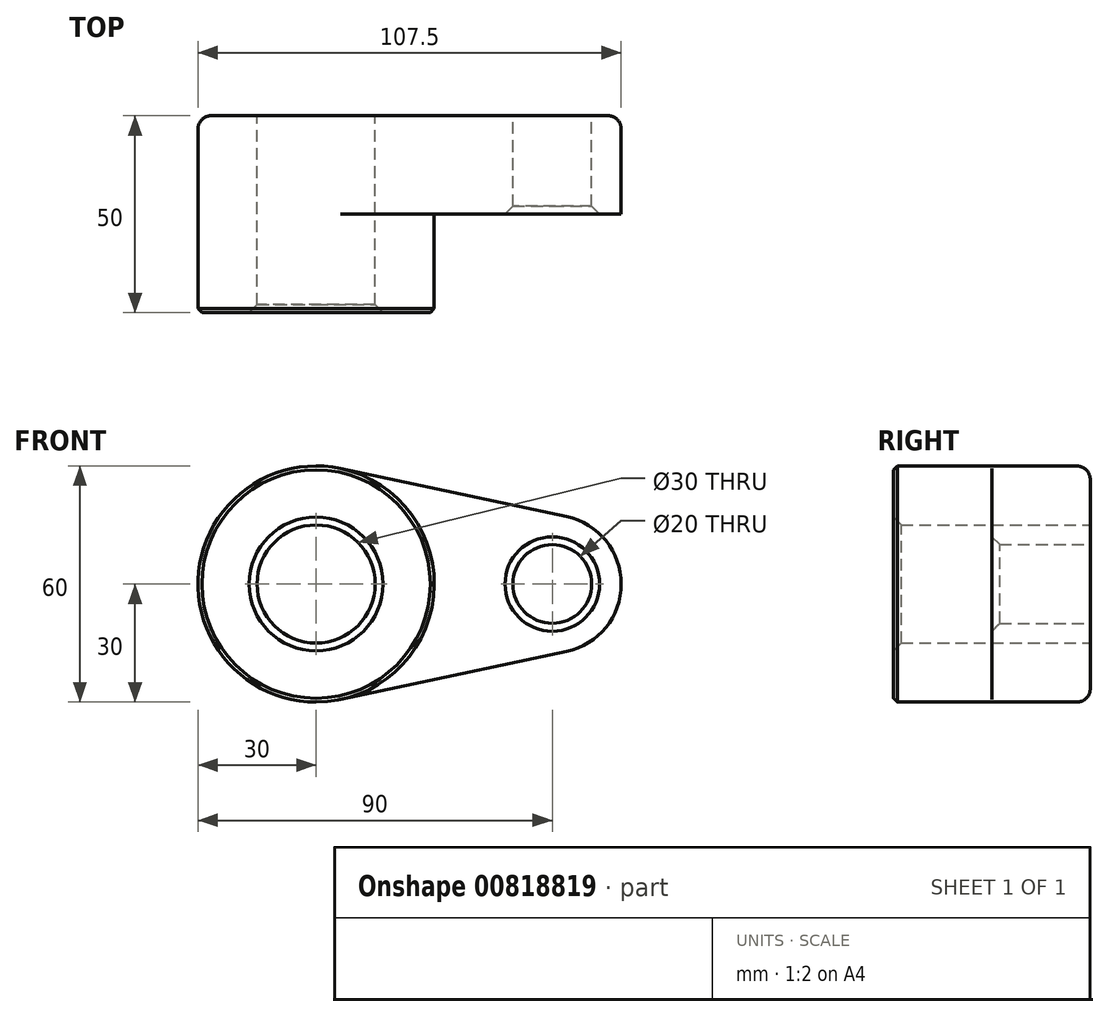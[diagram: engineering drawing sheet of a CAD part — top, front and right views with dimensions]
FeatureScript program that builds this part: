
annotation { "Feature Type Name" : "Feature", "Feature Type Description" : "" }
export const myFeature = defineFeature(function(context is Context, id is Id, definition is map)
    precondition{}
    {
        {
            var Q0;
            Q0=qCreatedBy(makeId("Front.planeOp"),FACE);
            var sketch = newSketch(context, id + "F0", { "sketchPlane" : qUnion([Q0])});
            skCircle(sketch, "E0", {"center": v(0, 0) * mm, "radius": 30 * mm});
            skCircle(sketch, "E1", {"center": v(60, 0) * mm, "radius": 17.5 * mm});
            skLineSegment(sketch, "E2", {"start": v(6.25, 29.34) * mm, "end": v(63.65, 17.12) * mm});
            skLineSegment(sketch, "E3", {"start": v(6.25, -29.34) * mm, "end": v(63.65, -17.12) * mm});
            skCircle(sketch, "E4", {"center": v(0, 0) * mm, "radius": 15 * mm});
            skCircle(sketch, "E5", {"center": v(60, 0) * mm, "radius": 10 * mm});
            skSolve(sketch);
        }
        {
            var Q0;
            Q0 = qSketchRegion(id + "F0", true);
            extrude(context, id + "F1", {"entities" : qUnion([Q0]), "depth" : 25 * mm, "offsetDistance" : 25 * mm});
        }
        {
            var Q0;
            Q0=makeQuery(id+"F0.imprint","IMPRINT",FACE,{"disambiguationData":[TD([[makeQuery(id+"F0.imprint","IMPRINT",EDGE,{"derivedFrom":sQuery(id+"F0.wireOp",EDGE,"E4")}),-1.0]])]});
            extrude(context, id + "F2", {"entities" : qUnion([Q0]), "operationType" : NewBodyOperationType.ADD, "depth" : 50 * mm, "offsetDistance" : 25 * mm});
        }
        {
            var Q0;
            Q0=makeQuery(id+"F1.opExtrude","CAP_EDGE",EDGE,{"disambiguationData":[OSD([sQuery(id+"F0.wireOp",EDGE,"E0")])],"isStart":true});
            var Q1;
            Q1=makeQuery(id+"F1.opExtrude","CAP_EDGE",EDGE,{"disambiguationData":[OSD([sQuery(id+"F0.wireOp",EDGE,"E3")])],"isStart":true});
            var Q2;
            Q2=makeQuery(id+"F1.opExtrude","CAP_EDGE",EDGE,{"disambiguationData":[OSD([sQuery(id+"F0.wireOp",EDGE,"E1")])],"isStart":true});
            var Q3;
            Q3=makeQuery(id+"F1.opExtrude","CAP_EDGE",EDGE,{"disambiguationData":[OSD([sQuery(id+"F0.wireOp",EDGE,"E2")])],"isStart":true});
            fillet(context, id + "F3", {"entities" : qUnion([Q0, Q1, Q2, Q3]), "radius" : 3.38 * mm, "tangentPropagation" : true, "allowEdgeOverflow" : false});
        }
        {
            var Q0;
            Q0=makeQuery(id+"F2.opExtrude","CAP_EDGE",EDGE,{"disambiguationData":[OSD([sQuery(id+"F0.wireOp",EDGE,"E4")])],"isStart":false});
            var Q1;
            Q1=makeQuery(id+"F1.opExtrude","CAP_EDGE",EDGE,{"disambiguationData":[OSD([sQuery(id+"F0.wireOp",EDGE,"E5")])],"isStart":false});
            chamfer(context, id + "F4", {"entities" : qUnion([Q0, Q1]), "width" : 2 * mm, "tangentPropagation" : true});
        }
        {
            var Q0;
            Q0=makeQuery(id+"F2.opExtrude","CAP_EDGE",EDGE,{"disambiguationData":[OSD([sQuery(id+"F0.wireOp",EDGE,"E0")])],"isStart":false});
            chamfer(context, id + "F5", {"entities" : qUnion([Q0]), "width" : 1 * mm, "tangentPropagation" : true});
        }
    });
